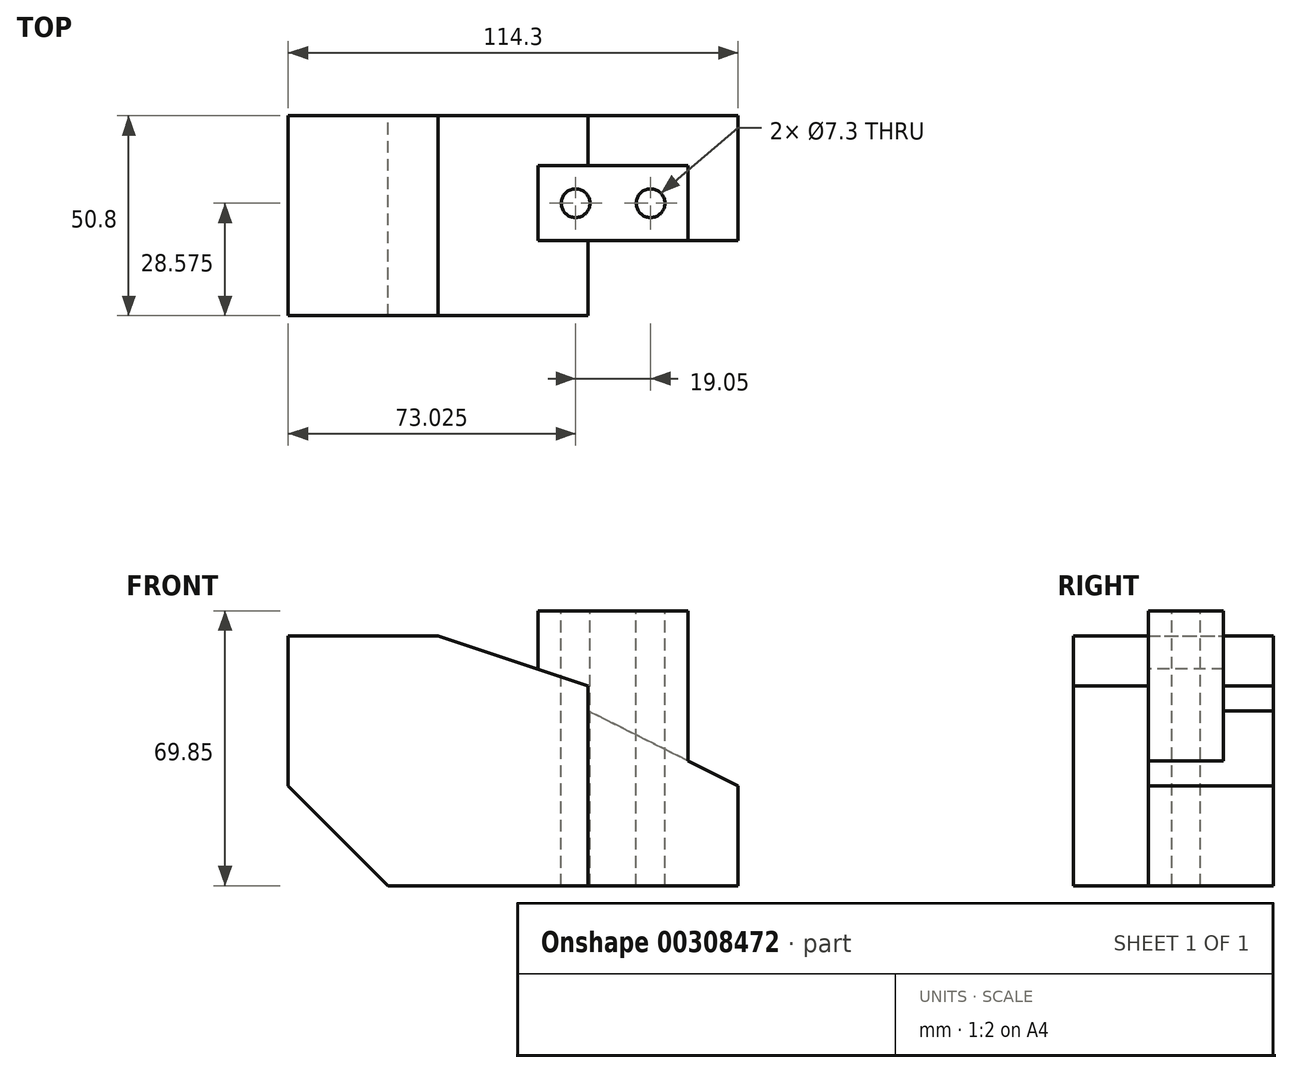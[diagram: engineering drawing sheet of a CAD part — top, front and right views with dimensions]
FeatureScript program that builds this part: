
annotation { "Feature Type Name" : "Feature", "Feature Type Description" : "" }
export const myFeature = defineFeature(function(context is Context, id is Id, definition is map)
    precondition{}
    {
        {
            var Q0;
            Q0=qCreatedBy(makeId("Front.planeOp"),FACE);
            var sketch = newSketch(context, id + "F0", { "sketchPlane" : qUnion([Q0])});
            skLineSegment(sketch, "E0", {"start": v(38.1, 0) * mm, "end": v(-12.7, 0) * mm});
            skLineSegment(sketch, "E1", {"start": v(38.1, 0) * mm, "end": v(38.1, 50.8) * mm});
            skLineSegment(sketch, "E2", {"start": v(0, 63.5) * mm, "end": v(-38.1, 63.5) * mm});
            skLineSegment(sketch, "E3", {"start": v(0, 63.5) * mm, "end": v(38.1, 50.8) * mm});
            skLineSegment(sketch, "E4", {"start": v(-38.1, 63.5) * mm, "end": v(-38.1, 25.4) * mm});
            skLineSegment(sketch, "E5", {"start": v(-38.1, 25.4) * mm, "end": v(-12.7, 0) * mm});
            skLineSegment(sketch, "E6", {"start": v(38.1, 0) * mm, "end": v(76.2, 0) * mm});
            skLineSegment(sketch, "E7", {"start": v(76.2, 0) * mm, "end": v(76.2, 25.4) * mm});
            skLineSegment(sketch, "E8", {"start": v(63.5, 31.75) * mm, "end": v(76.2, 25.4) * mm});
            skLineSegment(sketch, "E9", {"start": v(63.5, 31.75) * mm, "end": v(63.5, 50.8) * mm});
            skLineSegment(sketch, "E10", {"start": v(63.5, 50.8) * mm, "end": v(38.1, 50.8) * mm});
            skSolve(sketch);
        }
        {
            var Q0;
            Q0 = qSketchRegion(id + "F0", true);
            extrude(context, id + "F1", {"entities" : qUnion([Q0]), "depth" : 50.8 * mm});
        }
        {
            var Q0;
            Q0=makeQuery(id+"F1.opExtrude","CAP_FACE",FACE,{"disambiguationData":[OSD([sQuery(id+"F0.wireOp",EDGE,"E0"),sQuery(id+"F0.wireOp",EDGE,"E2"),sQuery(id+"F0.wireOp",EDGE,"E3"),sQuery(id+"F0.wireOp",EDGE,"E4"),sQuery(id+"F0.wireOp",EDGE,"E5"),sQuery(id+"F0.wireOp",EDGE,"E6"),sQuery(id+"F0.wireOp",EDGE,"E7"),sQuery(id+"F0.wireOp",EDGE,"E8"),sQuery(id+"F0.wireOp",EDGE,"E9"),sQuery(id+"F0.wireOp",EDGE,"E10")])],"isStart":false});
            var sketch = newSketch(context, id + "F2", { "sketchPlane" : qUnion([Q0])});
            skLineSegment(sketch, "E11", {"start": v(38.1, 50.8) * mm, "end": v(38.1, 0) * mm});
            skLineSegment(sketch, "E12", {"start": v(38.1, 0) * mm, "end": v(76.2, 0) * mm});
            skLineSegment(sketch, "E13", {"start": v(76.2, 0) * mm, "end": v(76.2, 25.4) * mm});
            skLineSegment(sketch, "E14", {"start": v(76.2, 25.4) * mm, "end": v(63.5, 31.75) * mm});
            skLineSegment(sketch, "E15", {"start": v(63.5, 31.75) * mm, "end": v(63.5, 50.8) * mm});
            skLineSegment(sketch, "E16", {"start": v(63.5, 50.8) * mm, "end": v(38.1, 50.8) * mm});
            skSolve(sketch);
        }
        {
            var Q0;
            Q0 = qSketchRegion(id + "F2", true);
            extrude(context, id + "F3", {"entities" : qUnion([Q0]), "operationType" : NewBodyOperationType.REMOVE, "oppositeDirection" : true, "depth" : 19.05 * mm});
        }
        {
            var Q0;
            Q0=makeQuery(id+"F1.opExtrude","CAP_FACE",FACE,{"disambiguationData":[OSD([sQuery(id+"F0.wireOp",EDGE,"E0"),sQuery(id+"F0.wireOp",EDGE,"E2"),sQuery(id+"F0.wireOp",EDGE,"E3"),sQuery(id+"F0.wireOp",EDGE,"E4"),sQuery(id+"F0.wireOp",EDGE,"E5"),sQuery(id+"F0.wireOp",EDGE,"E6"),sQuery(id+"F0.wireOp",EDGE,"E7"),sQuery(id+"F0.wireOp",EDGE,"E8"),sQuery(id+"F0.wireOp",EDGE,"E9"),sQuery(id+"F0.wireOp",EDGE,"E10")])],"isStart":true});
            var sketch = newSketch(context, id + "F4", { "sketchPlane" : qUnion([Q0])});
            skLineSegment(sketch, "E17", {"start": v(-76.2, 25.4) * mm, "end": v(-38.1, 44.45) * mm});
            skLineSegment(sketch, "E18", {"start": v(-38.1, 44.45) * mm, "end": v(-38.1, 50.8) * mm});
            skLineSegment(sketch, "E19", {"start": v(-38.1, 50.8) * mm, "end": v(-63.5, 50.8) * mm});
            skLineSegment(sketch, "E20", {"start": v(-63.5, 50.8) * mm, "end": v(-63.5, 31.75) * mm});
            skSolve(sketch);
        }
        {
            var Q0;
            Q0 = qSketchRegion(id + "F4", true);
            extrude(context, id + "F5", {"entities" : qUnion([Q0]), "operationType" : NewBodyOperationType.REMOVE, "oppositeDirection" : true, "depth" : 12.7 * mm});
        }
        {
            var Q0;
            Q0=makeQuery(id+"F1.opExtrude","SWEPT_FACE",FACE,{"disambiguationData":[OSD([sQuery(id+"F0.wireOp",EDGE,"E10")])]});
            var sketch = newSketch(context, id + "F6", { "sketchPlane" : qUnion([Q0])});
            skLineSegment(sketch, "E21", {"start": v(63.5, -12.7) * mm, "end": v(63.5, -31.75) * mm});
            skLineSegment(sketch, "E22", {"start": v(63.5, -31.75) * mm, "end": v(25.4, -31.75) * mm});
            skLineSegment(sketch, "E23", {"start": v(25.4, -31.75) * mm, "end": v(25.4, -12.7) * mm});
            skLineSegment(sketch, "E24", {"start": v(25.4, -12.7) * mm, "end": v(63.5, -12.7) * mm});
            skSolve(sketch);
        }
        {
            var Q0;
            Q0 = qSketchRegion(id + "F6", true);
            extrude(context, id + "F7", {"entities" : qUnion([Q0]), "operationType" : NewBodyOperationType.ADD, "depth" : 19.05 * mm});
        }
        {
            var Q0;
            Q0=makeQuery(id+"F7.opExtrude","CAP_FACE",FACE,{"disambiguationData":[OSD([sQuery(id+"F6.wireOp",EDGE,"E21"),sQuery(id+"F6.wireOp",EDGE,"E22"),sQuery(id+"F6.wireOp",EDGE,"E23"),sQuery(id+"F6.wireOp",EDGE,"E24")])],"isStart":false});
            var sketch = newSketch(context, id + "F8", { "sketchPlane" : qUnion([Q0])});
            skCircle(sketch, "E25", {"center": v(34.92, -22.23) * mm, "radius": 3.65 * mm});
            skCircle(sketch, "E26", {"center": v(53.97, -22.23) * mm, "radius": 3.65 * mm});
            skSolve(sketch);
        }
        {
            var Q0;
            Q0 = qSketchRegion(id + "F8", true);
            extrude(context, id + "F9", {"entities" : qUnion([Q0]), "operationType" : NewBodyOperationType.REMOVE, "endBound" : BoundingType.THROUGH_ALL, "oppositeDirection" : true, "depth" : 25.4 * mm});
        }
    });
